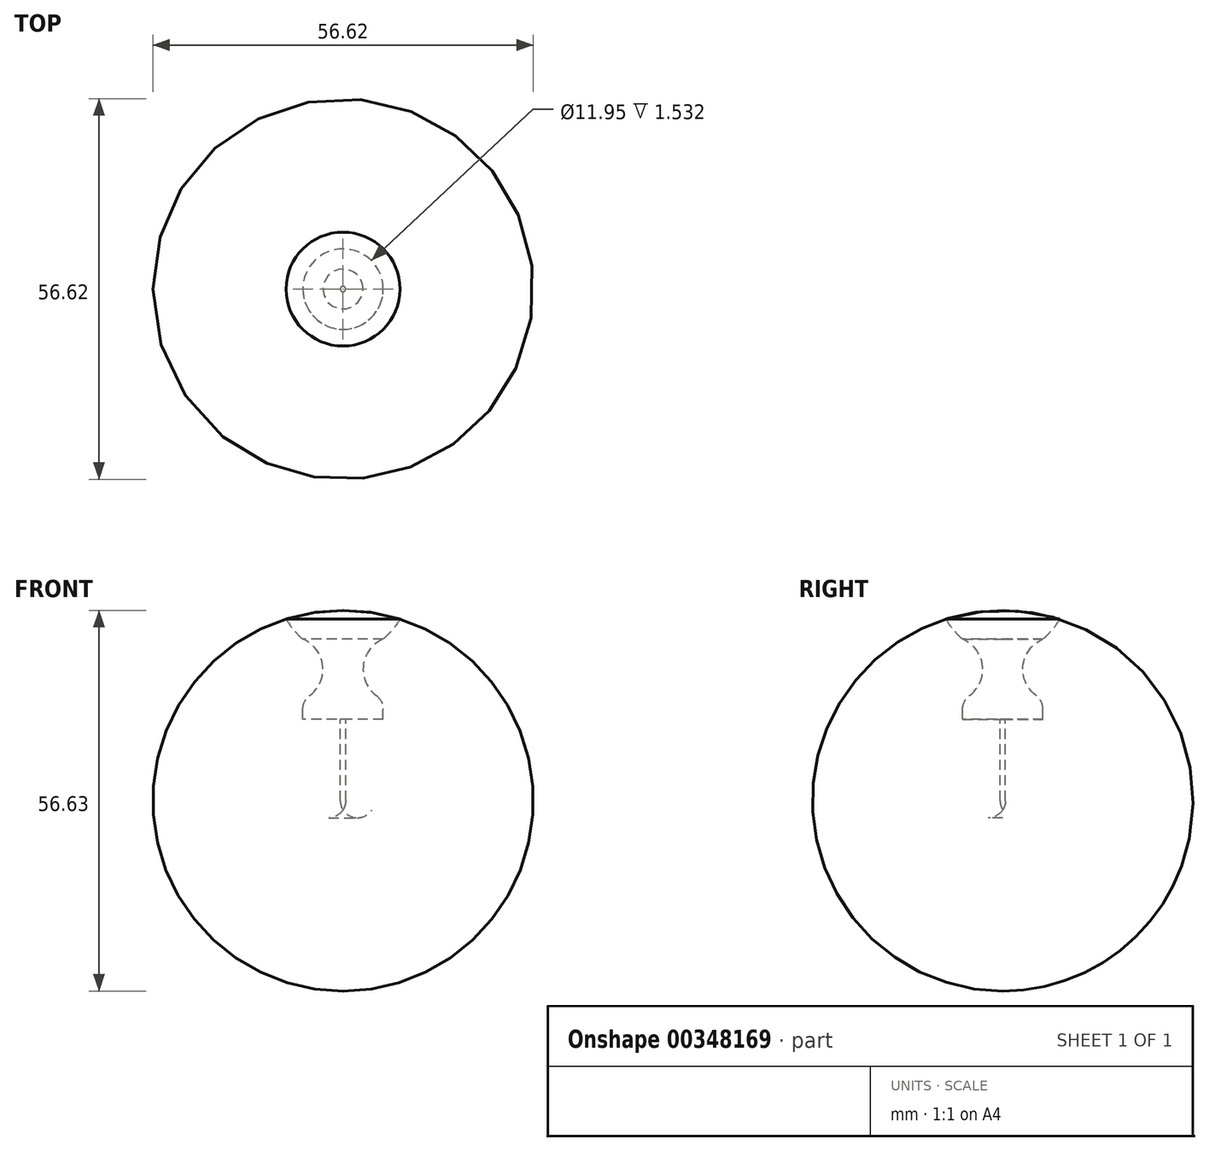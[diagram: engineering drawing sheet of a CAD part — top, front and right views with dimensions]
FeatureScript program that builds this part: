
annotation { "Feature Type Name" : "Feature", "Feature Type Description" : "" }
export const myFeature = defineFeature(function(context is Context, id is Id, definition is map)
    precondition{}
    {
        {
            var Q0;
            Q0=qCreatedBy(makeId("Front.planeOp"),FACE);
            var sketch = newSketch(context, id + "F0", { "sketchPlane" : qUnion([Q0])});
            skLineSegment(sketch, "E0", {"start": v(0, 7.47) * mm, "end": v(0, -7.47) * mm});
            skLineSegment(sketch, "E1", {"start": v(0, 7.47) * mm, "end": v(8.47, 7.47) * mm});
            skLineSegment(sketch, "E2", {"start": v(0, -7.47) * mm, "end": v(5.98, -7.47) * mm});
            skLineSegment(sketch, "E3", {"start": v(5.98, -7.47) * mm, "end": v(5.98, -4.48) * mm});
            skLineSegment(sketch, "E4", {"start": v(0, 0) * mm, "end": v(2.99, 0) * mm, "construction": true});
            skArc(sketch, "E5", {"start": v(5.98, 4.48) * mm, "mid": v(2.99, 0) * mm, "end": v(5.98, -4.48) * mm});
            skLineSegment(sketch, "E6", {"start": v(5.98, 4.48) * mm, "end": v(5.98, -4.48) * mm, "construction": true});
            skArc(sketch, "E7", {"start": v(5.98, 4.48) * mm, "mid": v(7.35, 5.87) * mm, "end": v(8.47, 7.47) * mm});
            skLineSegment(sketch, "E8", {"start": v(0, -7.47) * mm, "end": v(0, -20.92) * mm});
            skLineSegment(sketch, "E9", {"start": v(0, -7.47) * mm, "end": v(0.4, -7.47) * mm, "construction": true});
            skLineSegment(sketch, "E10", {"start": v(0.4, -7.47) * mm, "end": v(0.4, -19.55) * mm});
            skArc(sketch, "E11", {"start": v(0, -20.92) * mm, "mid": v(0.3, -20.26) * mm, "end": v(0.4, -19.55) * mm});
            skLineSegment(sketch, "E12", {"start": v(8.47, 7.47) * mm, "end": v(-8.45, 7.47) * mm, "construction": true});
            skArc(sketch, "E13", {"start": v(8.47, 7.47) * mm, "mid": v(4.28, 8.44) * mm, "end": v(0, 8.76) * mm});
            skLineSegment(sketch, "E14", {"start": v(0, 8.76) * mm, "end": v(0, 7.47) * mm});
            skSolve(sketch);
        }
        {
            var Q0;
            Q0 = qSketchRegion(id + "F0", true);
            var Q1;
            Q1=sQuery(id+"F0.wireOp",EDGE,"E0");
            revolve(context, id + "F1", {"entities" : qUnion([Q0]), "axis" : qUnion([Q1]), "revolveType" : RevolveType.FULL});
        }
        {
            var Q0;
            Q0=makeQuery(id+"F1.opRevolve","SWEPT_EDGE",EDGE,{"disambiguationData":[OSD([sQuery(id+"F0.wireOp",EDGE,"E3"),sQuery(id+"F0.wireOp",EDGE,"E5")])]});
            fillet(context, id + "F2", {"entities" : qUnion([Q0]), "radius" : 2.54 * mm, "tangentPropagation" : true, "allowEdgeOverflow" : false});
        }
    });
